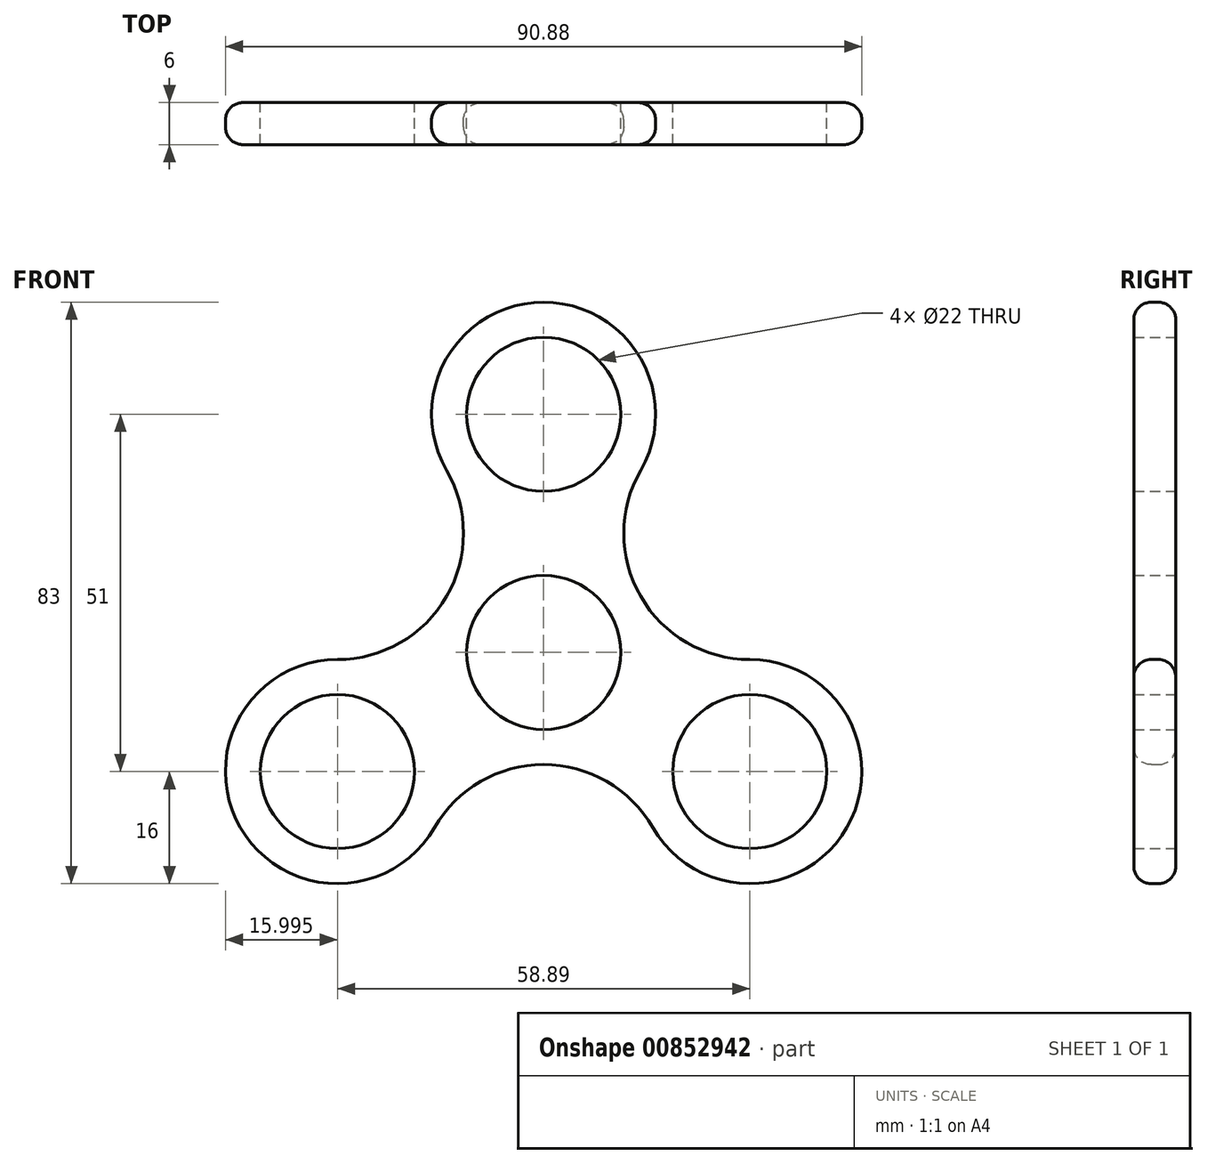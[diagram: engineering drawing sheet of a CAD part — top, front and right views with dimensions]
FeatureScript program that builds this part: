
annotation { "Feature Type Name" : "Feature", "Feature Type Description" : "" }
export const myFeature = defineFeature(function(context is Context, id is Id, definition is map)
    precondition{}
    {
        {
            var Q0;
            Q0=qCreatedBy(makeId("Front.planeOp"),FACE);
            var sketch = newSketch(context, id + "F0", { "sketchPlane" : qUnion([Q0])});
            skCircle(sketch, "E0", {"center": v(0, 0) * mm, "radius": 11 * mm});
            skCircle(sketch, "E1", {"center": v(0, 34) * mm, "radius": 11 * mm});
            skCircle(sketch, "E2", {"center": v(29.44, -17) * mm, "radius": 11 * mm});
            skCircle(sketch, "E3", {"center": v(-29.44, -17) * mm, "radius": 11 * mm});
            skCircle(sketch, "E4", {"center": v(0, 34) * mm, "radius": 16 * mm});
            skCircle(sketch, "E5", {"center": v(29.44, -17) * mm, "radius": 16 * mm});
            skCircle(sketch, "E6", {"center": v(-29.44, -17) * mm, "radius": 16 * mm});
            skCircle(sketch, "E7", {"center": v(0, 0) * mm, "radius": 16 * mm});
            skArc(sketch, "E8", {"start": v(13.86, 26) * mm, "mid": v(11.44, 17) * mm, "end": v(13.86, 8) * mm});
            skArc(sketch, "E9", {"start": v(-13.86, 26) * mm, "mid": v(-11.44, 17) * mm, "end": v(-13.86, 8) * mm});
            skArc(sketch, "E10", {"start": v(-13.86, 8) * mm, "mid": v(-20.44, 1.41) * mm, "end": v(-29.44, -1) * mm});
            skArc(sketch, "E11", {"start": v(0, -16) * mm, "mid": v(-9, -18.41) * mm, "end": v(-15.59, -25) * mm});
            skArc(sketch, "E12", {"start": v(0, -16) * mm, "mid": v(9, -18.41) * mm, "end": v(15.59, -25) * mm});
            skArc(sketch, "E13", {"start": v(29.44, -1) * mm, "mid": v(20.44, 1.41) * mm, "end": v(13.86, 8) * mm});
            skSolve(sketch);
        }
        {
            var Q0;
            Q0 = qSketchRegion(id + "F0", true);
            extrude(context, id + "F1", {"entities" : qUnion([Q0]), "endBound" : BoundingType.SYMMETRIC, "depth" : 6 * mm, "offsetDistance" : 25 * mm});
        }
        {
            var Q0;
            Q0=makeQuery(id+"F1.opExtrude","CAP_EDGE",EDGE,{"disambiguationData":[OSD([sQuery(id+"F0.wireOp",EDGE,"E4")])],"isStart":false});
            fillet(context, id + "F2", {"entities" : qUnion([Q0]), "radius" : 2.5 * mm, "tangentPropagation" : true, "allowEdgeOverflow" : false});
        }
        {
            var Q0;
            Q0=makeQuery(id+"F1.opExtrude","CAP_EDGE",EDGE,{"disambiguationData":[OSD([sQuery(id+"F0.wireOp",EDGE,"E8"),sQuery(id+"F0.wireOp",EDGE,"E13")])],"isStart":true});
            fillet(context, id + "F3", {"entities" : qUnion([Q0]), "radius" : 2.5 * mm, "tangentPropagation" : true, "allowEdgeOverflow" : false});
        }
    });
